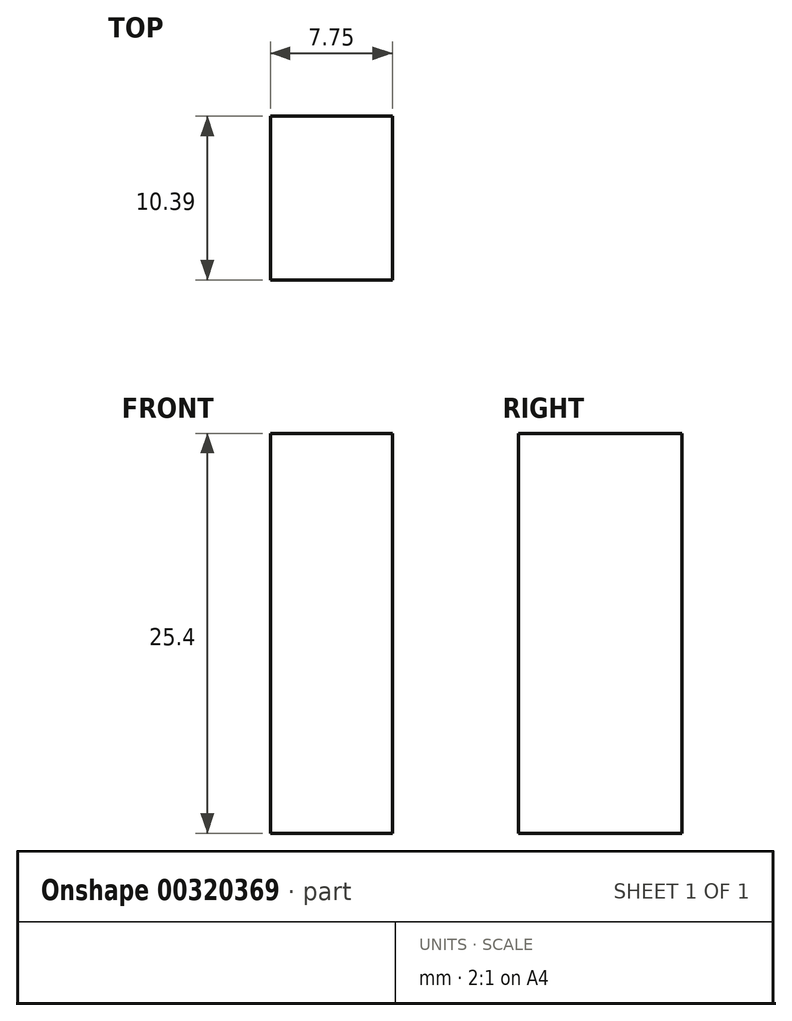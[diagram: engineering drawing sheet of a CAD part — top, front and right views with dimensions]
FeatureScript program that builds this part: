
annotation { "Feature Type Name" : "Feature", "Feature Type Description" : "" }
export const myFeature = defineFeature(function(context is Context, id is Id, definition is map)
    precondition{}
    {
        {
            var Q0;
            Q0=qCreatedBy(makeId("Top.planeOp"),FACE);
            var sketch = newSketch(context, id + "F0", { "sketchPlane" : qUnion([Q0])});
            skLineSegment(sketch, "E0.bottom", {"start": v(-42.8, 18.65) * mm, "end": v(30.78, 18.65) * mm});
            skLineSegment(sketch, "E0.top", {"start": v(-42.8, -25.79) * mm, "end": v(30.78, -25.79) * mm});
            skLineSegment(sketch, "E0.left", {"start": v(-42.8, 18.65) * mm, "end": v(-42.8, -25.79) * mm});
            skLineSegment(sketch, "E0.right", {"start": v(30.78, 18.65) * mm, "end": v(30.78, -25.79) * mm});
            skLineSegment(sketch, "E1.bottom", {"start": v(-4.9, 24.16) * mm, "end": v(-12.64, 24.16) * mm});
            skLineSegment(sketch, "E1.top", {"start": v(-4.9, 34.55) * mm, "end": v(-12.64, 34.55) * mm});
            skLineSegment(sketch, "E1.left", {"start": v(-4.9, 24.16) * mm, "end": v(-4.9, 34.55) * mm});
            skLineSegment(sketch, "E1.right", {"start": v(-12.64, 24.16) * mm, "end": v(-12.64, 34.55) * mm});
            skSolve(sketch);
        }
        {
            var Q0;
            Q0=makeQuery(id+"F0.imprint","IMPRINT",FACE,{"disambiguationData":[TD([[makeQuery(id+"F0.imprint","IMPRINT",EDGE,{"derivedFrom":sQuery(id+"F0.wireOp",EDGE,"E1.bottom")}),-1.0]])]});
            extrude(context, id + "F1", {"entities" : qUnion([Q0]), "depth" : 25.4 * mm});
        }
    });
